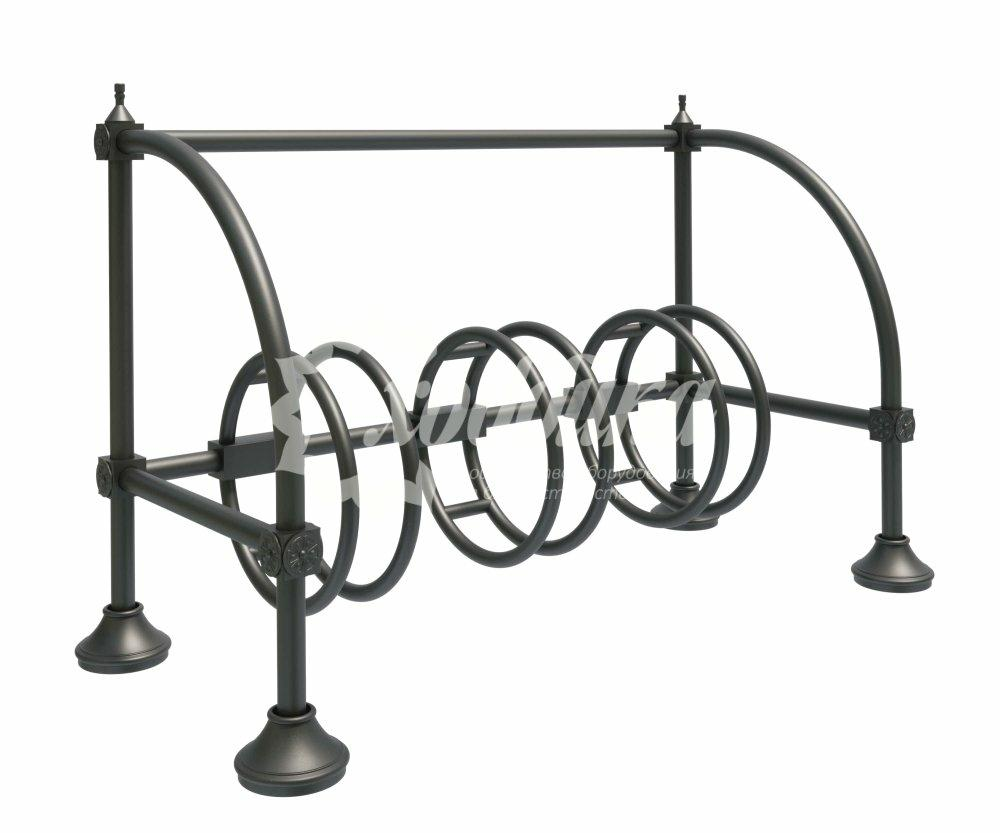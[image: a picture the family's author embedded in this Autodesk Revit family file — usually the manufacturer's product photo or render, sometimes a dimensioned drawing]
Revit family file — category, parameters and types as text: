
# Revit family: 12317 Велопарковка чугунная Хоббика
name_source: partatom
category: Антураж
revit_build: Autodesk Revit 2018 (Build: 20180423_1000(x64)
units: mm (PartAtom-declared; Revit-internal decimal feet)

## family parameters
Всегда вертикально = Да
Источник визуального образа = Геометрия семейства
На основе рабочей плоскости = Нет
Общий = Нет
При загрузке вырезать с полостями = Нет
Точка расчета площади = Нет

## types (2) — shared parameters
URL = https://hobbyka.ru
Артикул товара = Арт. 12317
Высота = 1100 мм
Группа модели = Велопарковки
Изготовитель = ООО «Хоббика»
Материал изделия = Чугун
Цвет каркаса = Чугун
Ширина = 640 мм

## per-type parameters (varying)
| type | 3 места | 4 места | Длина | Изображение типоразмера | Описание |
| 3 места | Да | Нет | 1525 мм | Велопарковка чугунная Арт 12317 на 3 места.jpg | Велопарковка чугунная. Версия на 3 места |
| 4 места | Нет | Да | 2000 мм | Велопарковка чугунная Арт 12317 на 4 места.jpg | Велопарковка чугунная. Версия на 4 места |
